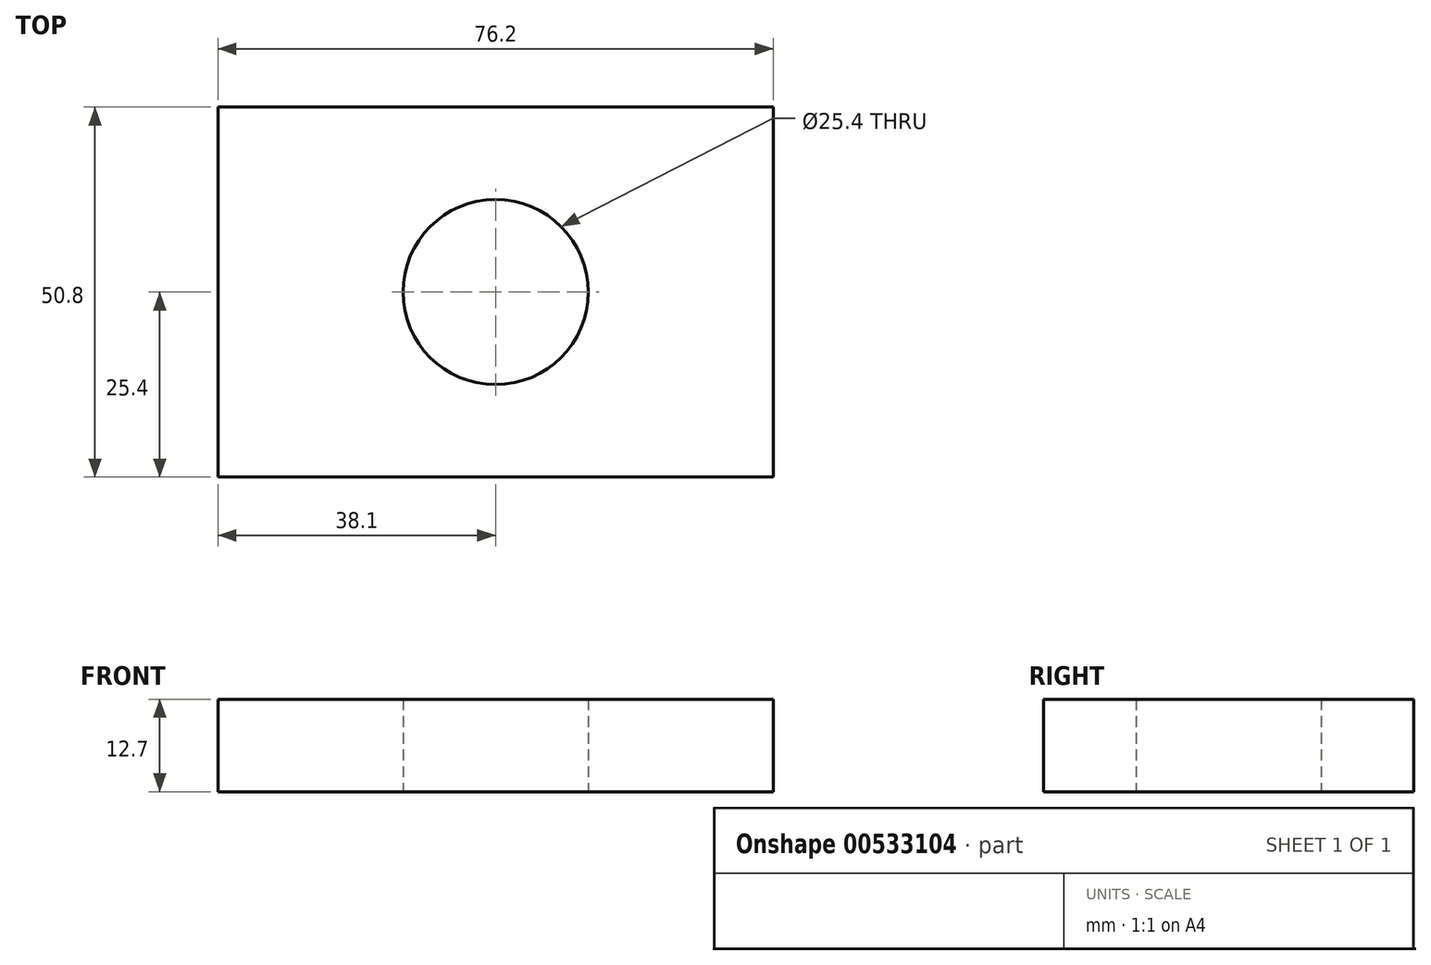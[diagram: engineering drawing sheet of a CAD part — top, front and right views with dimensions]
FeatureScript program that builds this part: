
annotation { "Feature Type Name" : "Feature", "Feature Type Description" : "" }
export const myFeature = defineFeature(function(context is Context, id is Id, definition is map)
    precondition{}
    {
        {
            var Q0;
            Q0=qCreatedBy(makeId("Top.planeOp"),FACE);
            var sketch = newSketch(context, id + "F0", { "sketchPlane" : qUnion([Q0])});
            skLineSegment(sketch, "E0.bottom", {"start": v(38.1, 25.4) * mm, "end": v(-38.1, 25.4) * mm});
            skLineSegment(sketch, "E0.top", {"start": v(38.1, -25.4) * mm, "end": v(-38.1, -25.4) * mm});
            skLineSegment(sketch, "E0.left", {"start": v(38.1, 25.4) * mm, "end": v(38.1, -25.4) * mm});
            skLineSegment(sketch, "E0.right", {"start": v(-38.1, 25.4) * mm, "end": v(-38.1, -25.4) * mm});
            skPoint(sketch, "E0.middle", {"position": v(0, 0) * mm});
            skCircle(sketch, "E1", {"center": v(0, 0) * mm, "radius": 12.7 * mm});
            skSolve(sketch);
        }
        {
            var Q0;
            Q0=makeQuery(id+"F0.imprint","IMPRINT",FACE,{"disambiguationData":[TD([[makeQuery(id+"F0.imprint","IMPRINT",EDGE,{"derivedFrom":sQuery(id+"F0.wireOp",EDGE,"E0.bottom")}),1.0]])]});
            extrude(context, id + "F1", {"entities" : qUnion([Q0]), "depth" : 12.7 * mm, "offsetDistance" : 25.4 * mm});
        }
    });
